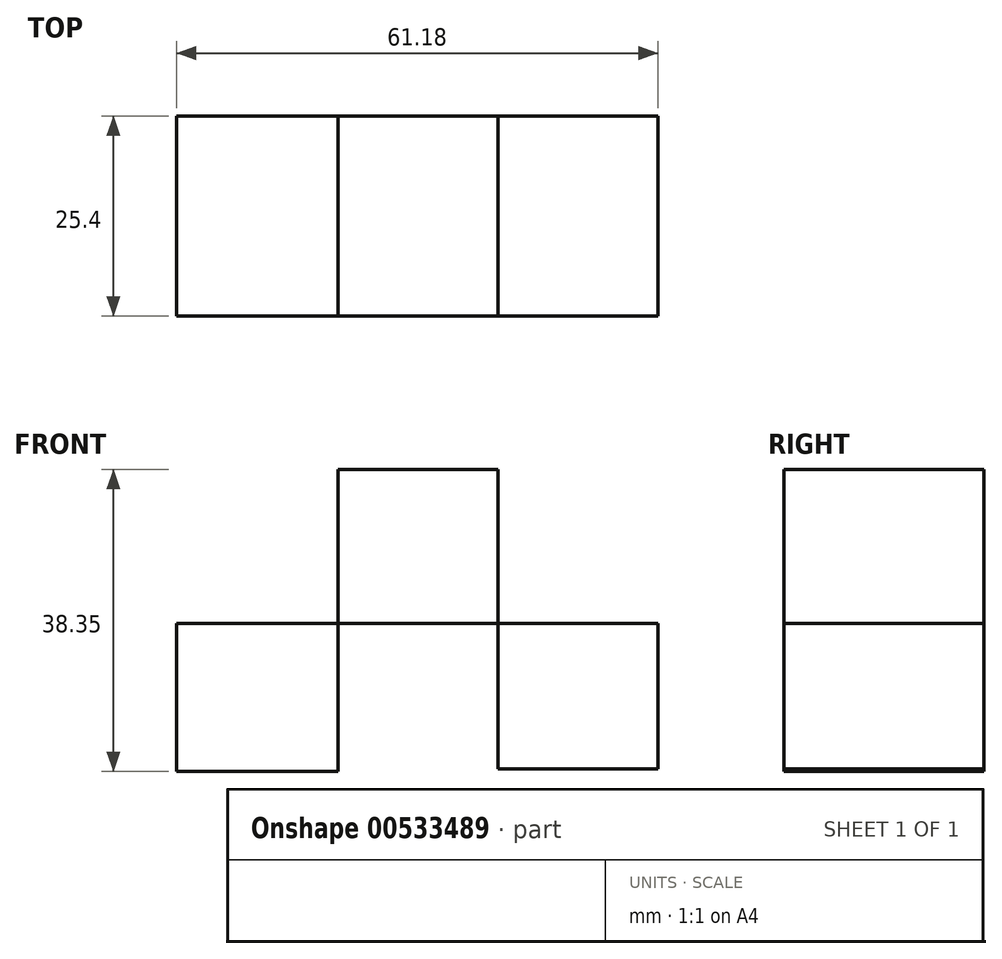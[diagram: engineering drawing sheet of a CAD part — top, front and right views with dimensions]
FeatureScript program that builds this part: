
annotation { "Feature Type Name" : "Feature", "Feature Type Description" : "" }
export const myFeature = defineFeature(function(context is Context, id is Id, definition is map)
    precondition{}
    {
        {
            var Q0;
            Q0=qCreatedBy(makeId("Front.planeOp"),FACE);
            var sketch = newSketch(context, id + "F0", { "sketchPlane" : qUnion([Q0])});
            skLineSegment(sketch, "E0.bottom", {"start": v(10.16, 16.02) * mm, "end": v(-10.16, 16.02) * mm});
            skLineSegment(sketch, "E0.top", {"start": v(10.16, 35.54) * mm, "end": v(-10.16, 35.54) * mm});
            skLineSegment(sketch, "E0.left", {"start": v(10.16, 16.02) * mm, "end": v(10.16, 35.54) * mm});
            skLineSegment(sketch, "E0.right", {"start": v(-10.16, 16.02) * mm, "end": v(-10.16, 35.54) * mm});
            skPoint(sketch, "E0.middle", {"position": v(0, 25.78) * mm});
            skLineSegment(sketch, "E1.bottom", {"start": v(-10.16, 16.02) * mm, "end": v(10.16, 16.02) * mm});
            skLineSegment(sketch, "E1.top", {"start": v(-10.16, -2.46) * mm, "end": v(10.16, -2.46) * mm});
            skLineSegment(sketch, "E1.left", {"start": v(-10.16, 16.02) * mm, "end": v(-10.16, -2.46) * mm});
            skLineSegment(sketch, "E1.right", {"start": v(10.16, 16.02) * mm, "end": v(10.16, -2.46) * mm});
            skLineSegment(sketch, "E2.bottom", {"start": v(-10.16, 16.02) * mm, "end": v(-30.67, 16.02) * mm});
            skLineSegment(sketch, "E2.top", {"start": v(-10.16, -2.81) * mm, "end": v(-30.67, -2.81) * mm});
            skLineSegment(sketch, "E2.left", {"start": v(-10.16, 16.02) * mm, "end": v(-10.16, -2.81) * mm});
            skLineSegment(sketch, "E2.right", {"start": v(-30.67, 16.02) * mm, "end": v(-30.67, -2.81) * mm});
            skLineSegment(sketch, "E3.bottom", {"start": v(10.16, -2.46) * mm, "end": v(30.51, -2.46) * mm});
            skLineSegment(sketch, "E3.top", {"start": v(10.16, 16.02) * mm, "end": v(30.51, 16.02) * mm});
            skLineSegment(sketch, "E3.left", {"start": v(10.16, -2.46) * mm, "end": v(10.16, 16.02) * mm});
            skLineSegment(sketch, "E3.right", {"start": v(30.51, -2.46) * mm, "end": v(30.51, 16.02) * mm});
            skSolve(sketch);
        }
        {
            var Q0;
            {var subQ0=sQuery(id+"F0.wireOp",EDGE,"E1.bottom");Q0=makeQuery(id+"F0.imprint","IMPRINT",FACE,{"disambiguationData":[TD([[makeQuery(id+"F0.imprint","IMPRINT",EDGE,{"derivedFrom":subQ0}),-1.0]])]});}
            var Q1;
            Q1=makeQuery(id+"F0.imprint","IMPRINT",FACE,{"disambiguationData":[TD([[makeQuery(id+"F0.imprint","IMPRINT",EDGE,{"derivedFrom":sQuery(id+"F0.wireOp",EDGE,"E0.top")}),1.0]])]});
            var Q2;
            Q2=makeQuery(id+"F0.imprint","IMPRINT",FACE,{"disambiguationData":[TD([[makeQuery(id+"F0.imprint","IMPRINT",EDGE,{"derivedFrom":sQuery(id+"F0.wireOp",EDGE,"E3.bottom")}),1.0]])]});
            var Q3;
            {var subQ3=sQuery(id+"F0.wireOp",EDGE,"E2.bottom");Q3=makeQuery(id+"F0.imprint","IMPRINT",FACE,{"disambiguationData":[TD([[makeQuery(id+"F0.imprint","IMPRINT",EDGE,{"derivedFrom":subQ3}),1.0]])]});}
            extrude(context, id + "F1", {"entities" : qUnion([Q0, Q1, Q2, Q3]), "depth" : 25.4 * mm, "offsetDistance" : 25.4 * mm});
        }
    });
